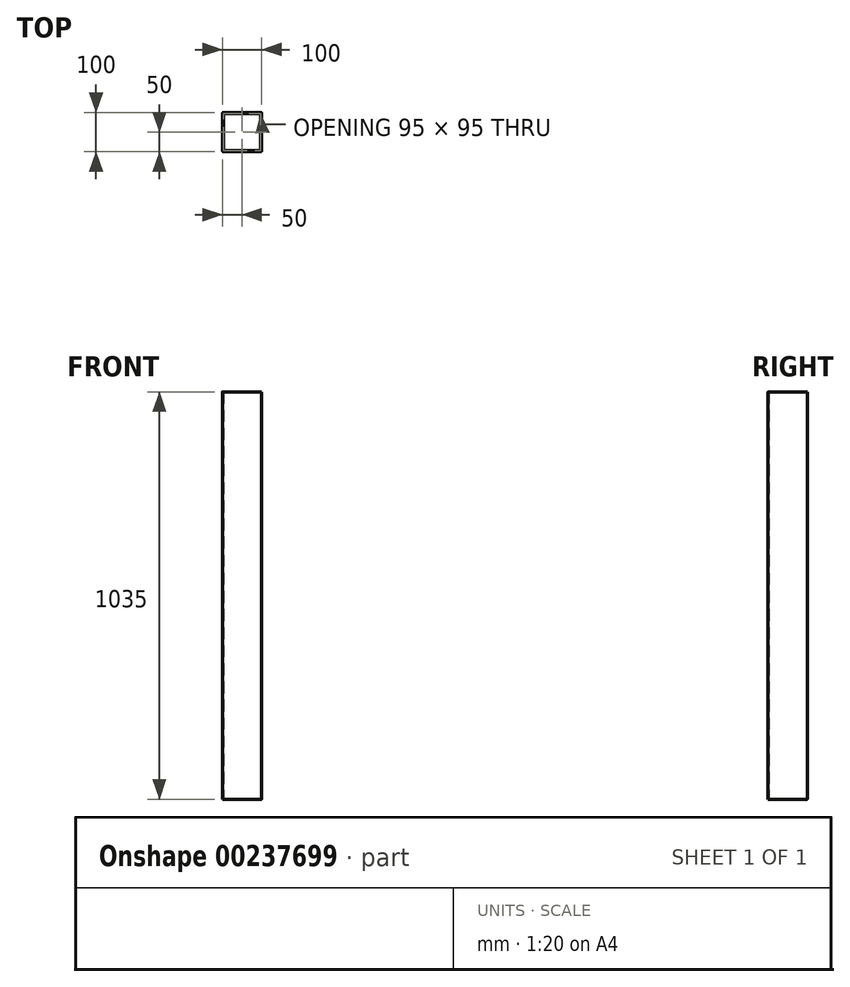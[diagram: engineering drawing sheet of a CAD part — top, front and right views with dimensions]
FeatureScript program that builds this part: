
annotation { "Feature Type Name" : "Feature", "Feature Type Description" : "" }
export const myFeature = defineFeature(function(context is Context, id is Id, definition is map)
    precondition{}
    {
        {
            var Q0;
            Q0=qCreatedBy(makeId("Top.planeOp"),FACE);
            var sketch = newSketch(context, id + "F0", { "sketchPlane" : qUnion([Q0])});
            skLineSegment(sketch, "E0.bottom", {"start": v(48, 50) * mm, "end": v(-48, 50) * mm});
            skLineSegment(sketch, "E0.top", {"start": v(48, -50) * mm, "end": v(-48, -50) * mm});
            skLineSegment(sketch, "E0.left", {"start": v(50, 48) * mm, "end": v(50, -48) * mm});
            skLineSegment(sketch, "E0.right", {"start": v(-50, 48) * mm, "end": v(-50, -48) * mm});
            skPoint(sketch, "E0.middle", {"position": v(0, 0) * mm});
            skPoint(sketch, "E1.visualSharp", {"position": v(-50, 50) * mm});
            skArc(sketch, "E1.filletArc", {"start": v(-48, 50) * mm, "mid": v(-49.41, 49.41) * mm, "end": v(-50, 48) * mm});
            skPoint(sketch, "E2.visualSharp", {"position": v(-50, -50) * mm});
            skArc(sketch, "E2.filletArc", {"start": v(-50, -48) * mm, "mid": v(-49.41, -49.41) * mm, "end": v(-48, -50) * mm});
            skPoint(sketch, "E3.visualSharp", {"position": v(50, -50) * mm});
            skArc(sketch, "E3.filletArc", {"start": v(48, -50) * mm, "mid": v(49.41, -49.41) * mm, "end": v(50, -48) * mm});
            skPoint(sketch, "E4.visualSharp", {"position": v(50, 50) * mm});
            skArc(sketch, "E4.filletArc", {"start": v(50, 48) * mm, "mid": v(49.41, 49.41) * mm, "end": v(48, 50) * mm});
            skLineSegment(sketch, "E5.bottom", {"start": v(46.5, 47.5) * mm, "end": v(-46.5, 47.5) * mm});
            skLineSegment(sketch, "E5.top", {"start": v(46.5, -47.5) * mm, "end": v(-46.5, -47.5) * mm});
            skLineSegment(sketch, "E5.left", {"start": v(47.5, 46.5) * mm, "end": v(47.5, -46.5) * mm});
            skLineSegment(sketch, "E5.right", {"start": v(-47.5, 46.5) * mm, "end": v(-47.5, -46.5) * mm});
            skPoint(sketch, "E6.visualSharp", {"position": v(47.5, 47.5) * mm});
            skArc(sketch, "E6.filletArc", {"start": v(47.5, 46.5) * mm, "mid": v(47.2, 47.2) * mm, "end": v(46.5, 47.5) * mm});
            skPoint(sketch, "E7.visualSharp", {"position": v(-47.5, 47.5) * mm});
            skArc(sketch, "E7.filletArc", {"start": v(-46.5, 47.5) * mm, "mid": v(-47.2, 47.2) * mm, "end": v(-47.5, 46.5) * mm});
            skPoint(sketch, "E8.visualSharp", {"position": v(-47.5, -47.5) * mm});
            skArc(sketch, "E8.filletArc", {"start": v(-47.5, -46.5) * mm, "mid": v(-47.2, -47.2) * mm, "end": v(-46.5, -47.5) * mm});
            skPoint(sketch, "E9.visualSharp", {"position": v(47.5, -47.5) * mm});
            skArc(sketch, "E9.filletArc", {"start": v(46.5, -47.5) * mm, "mid": v(47.2, -47.2) * mm, "end": v(47.5, -46.5) * mm});
            skSolve(sketch);
        }
        {
            var Q0;
            Q0=makeQuery(id+"F0.imprint","IMPRINT",FACE,{"disambiguationData":[TD([[makeQuery(id+"F0.imprint","IMPRINT",EDGE,{"derivedFrom":sQuery(id+"F0.wireOp",EDGE,"E0.bottom")}),1.0]])]});
            extrude(context, id + "F1", {"entities" : qUnion([Q0]), "depth" : 1035 * mm});
        }
    });
